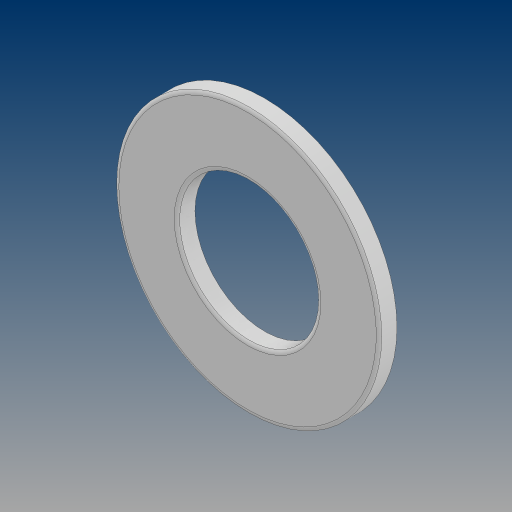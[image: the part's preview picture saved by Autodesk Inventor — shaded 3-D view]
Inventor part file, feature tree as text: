
AUTODESK INVENTOR PART (.ipt)
format: ipt  version: 2024.3 (Build 283343000, 343)  size: 127,488 bytes
history: native  units: in
note: dims shown in document units (in); Inventor stores cm internally (conversion verified against a paired STEP export)
features: fillet x1
ambient origin geometry x8: Origin, YZ Plane, XZ Plane, XY Plane, X Axis, Y Axis, Z Axis, Center Point
bodies: Solid1 (feature_tree)
feature tree (1):
  fillet  "Fillet1"  [1 undecoded]
note: 1 required parameter value undecoded (feature->parameter linkage not recoverable at this tier; creation-order binding heuristic only, values carry confidence <= 0.55)
